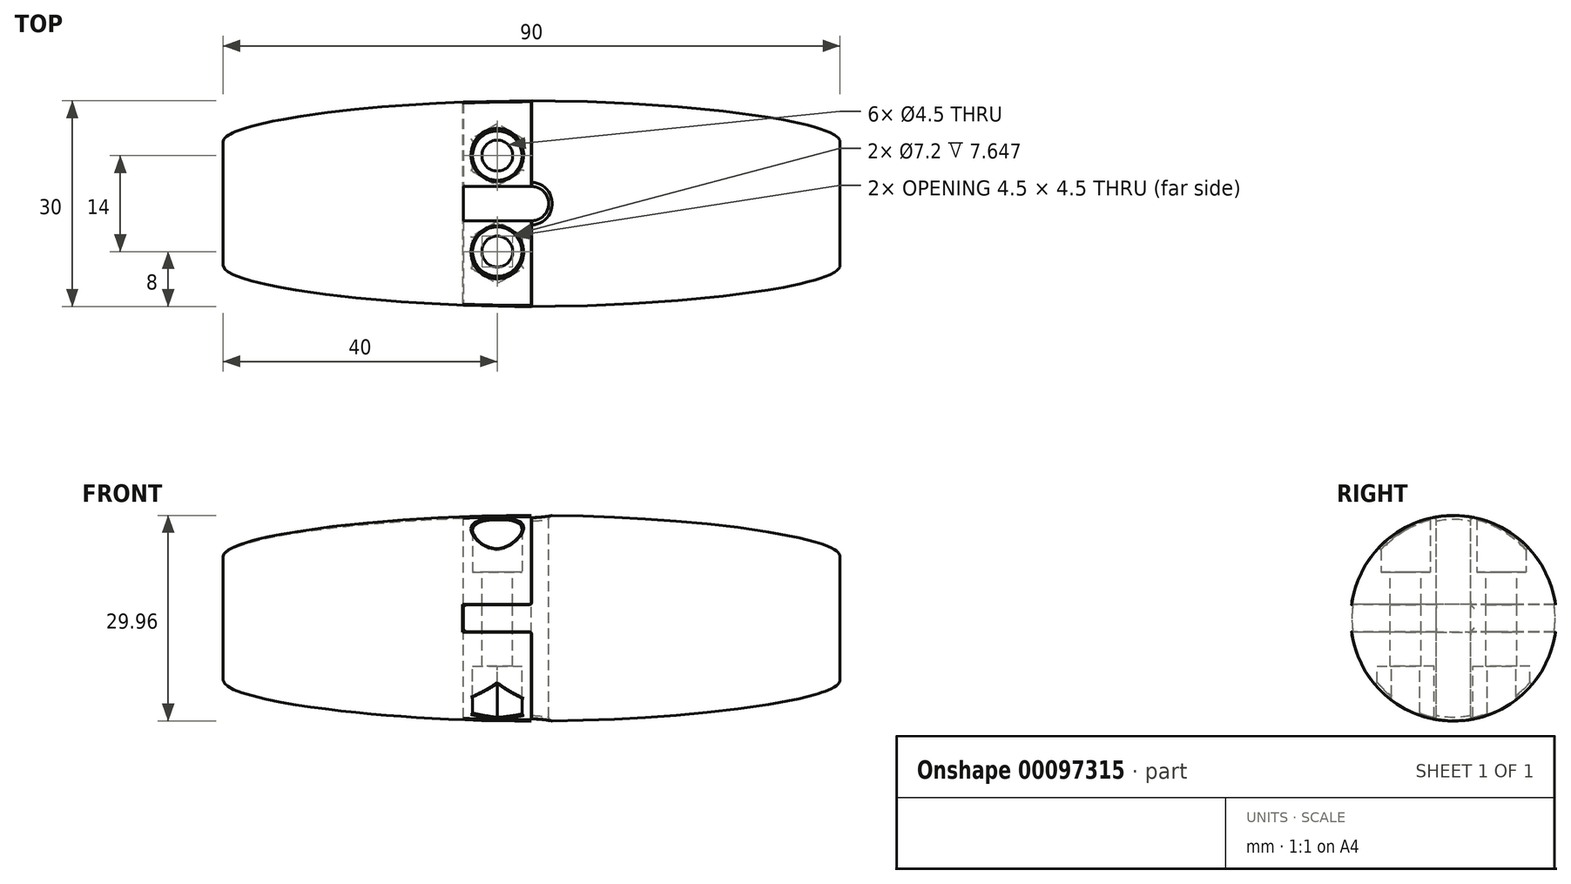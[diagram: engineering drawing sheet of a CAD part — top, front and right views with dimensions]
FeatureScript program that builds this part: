
annotation { "Feature Type Name" : "Feature", "Feature Type Description" : "" }
export const myFeature = defineFeature(function(context is Context, id is Id, definition is map)
    precondition{}
    {
        {
            assignVariable(context, id + "F0", {"name" : "rL", "anyValue" : 0.5});
        }
        {
            var Q0;
            Q0=qCreatedBy(makeId("Front.planeOp"),FACE);
            var sketch = newSketch(context, id + "F1", { "sketchPlane" : qUnion([Q0])});
            skLineSegment(sketch, "E0", {"start": v(0, 0) * mm, "end": v(45, 0) * mm});
            skLineSegment(sketch, "E1", {"start": v(45, 0) * mm, "end": v(45, 9) * mm});
            skLineSegment(sketch, "E2", {"start": v(0, 0) * mm, "end": v(0, 15) * mm, "construction": true});
            skLineSegment(sketch, "E3.MirrorCS", {"start": v(-45, 0) * mm, "end": v(-45, 9) * mm});
            skLineSegment(sketch, "E4.MirrorCS", {"start": v(0, 0) * mm, "end": v(-45, 0) * mm});
            skLineSegment(sketch, "E5", {"start": v(0, 15) * mm, "end": v(45, 15) * mm, "construction": true});
            skFitSpline(sketch, "E6", {"points": [v(-45, 9) * mm, v(0, 15) * mm, v(45, 9) * mm], "startDerivative": vector(0, 18) * mm, "endDerivative": vector(0, -18) * mm});
            skSolve(sketch);
        }
        {
            var Q0;
            Q0 = qSketchRegion(id + "F1", true);
            var Q1;
            Q1=sQuery(id+"F1.wireOp",EDGE,"E4.MirrorCS");
            revolve(context, id + "F2", {"entities" : qUnion([Q0]), "axis" : qUnion([Q1]), "revolveType" : RevolveType.FULL});
        }
        {
            var Q0;
            Q0=qCreatedBy(makeId("Top.planeOp"),FACE);
            var sketch = newSketch(context, id + "F3", { "sketchPlane" : qUnion([Q0])});
            skCircle(sketch, "E7", {"center": v(0, 0) * mm, "radius": 2.5 * mm});
            skSolve(sketch);
        }
        {
            var Q0;
            Q0 = qSketchRegion(id + "F3", true);
            extrude(context, id + "F4", {"entities" : qUnion([Q0]), "operationType" : NewBodyOperationType.REMOVE, "endBound" : BoundingType.THROUGH_ALL, "oppositeDirection" : true, "depth" : 25 * mm, "hasSecondDirection" : true, "secondDirectionBound" : SecondDirectionBoundingType.THROUGH_ALL, "secondDirectionOppositeDirection" : false, "secondDirectionDepth" : 25 * mm});
        }
        {
            var Q0;
            Q0=qCreatedBy(makeId("Front.planeOp"),FACE);
            var sketch = newSketch(context, id + "F5", { "sketchPlane" : qUnion([Q0])});
            skLineSegment(sketch, "E8", {"start": v(0, 14.99) * mm, "end": v(0, 2) * mm});
            skLineSegment(sketch, "E9", {"start": v(0, 2) * mm, "end": v(-10, 2) * mm});
            skLineSegment(sketch, "E10", {"start": v(-10, 2) * mm, "end": v(-10, -2) * mm});
            skLineSegment(sketch, "E11", {"start": v(-10, -2) * mm, "end": v(0, -2) * mm});
            skLineSegment(sketch, "E12", {"start": v(0, -2) * mm, "end": v(0, -14.99) * mm});
            skFitSpline(sketch, "E13", {"points": [v(45, -8) * mm, v(45, -11) * mm, v(0, -14) * mm, v(-45, -11) * mm, v(-45, -8) * mm], "construction": true});
            skFitSpline(sketch, "E14", {"points": [v(-45, 8) * mm, v(-45, 11) * mm, v(0, 14) * mm, v(45, 11) * mm, v(45, 8) * mm], "construction": true});
            skFitSpline(sketch, "E15", {"points": [v(-45, 8) * mm, v(-45, 11) * mm, v(0, 14) * mm, v(45, 11) * mm, v(45, 8) * mm], "construction": true});
            skFitSpline(sketch, "E16", {"points": [v(45, -8) * mm, v(45, -11) * mm, v(0, -14) * mm, v(-45, -11) * mm, v(-45, -8) * mm], "construction": true});
            skLineSegment(sketch, "E17.0", {"start": v(-0.05, -2.05) * mm, "end": v(-0.05, -14.99) * mm});
            skLineSegment(sketch, "E17.1", {"start": v(-0.05, 14.99) * mm, "end": v(-0.05, 2.05) * mm});
            skLineSegment(sketch, "E17.2", {"start": v(-0.05, 2.05) * mm, "end": v(-10.05, 2.05) * mm});
            skLineSegment(sketch, "E17.3", {"start": v(-10.05, 2.05) * mm, "end": v(-10.05, -2.05) * mm});
            skLineSegment(sketch, "E17.4", {"start": v(-10.05, -2.05) * mm, "end": v(-0.05, -2.05) * mm});
            skLineSegment(sketch, "E18.0", {"start": v(0.05, -1.95) * mm, "end": v(0.05, -14.99) * mm});
            skLineSegment(sketch, "E18.1", {"start": v(0.05, 14.99) * mm, "end": v(0.05, 1.95) * mm});
            skLineSegment(sketch, "E18.2", {"start": v(0.05, 1.95) * mm, "end": v(-9.95, 1.95) * mm});
            skLineSegment(sketch, "E18.3", {"start": v(-9.95, 1.95) * mm, "end": v(-9.95, -1.95) * mm});
            skLineSegment(sketch, "E18.4", {"start": v(-9.95, -1.95) * mm, "end": v(0.05, -1.95) * mm});
            skLineSegment(sketch, "E19", {"start": v(-0.05, -14.99) * mm, "end": v(0.05, -14.99) * mm});
            skLineSegment(sketch, "E20", {"start": v(-0.05, 14.99) * mm, "end": v(0.05, 14.99) * mm});
            skSolve(sketch);
        }
        {
            var Q0;
            Q0 = qSketchRegion(id + "F5", true);
            extrude(context, id + "F6", {"entities" : qUnion([Q0]), "operationType" : NewBodyOperationType.REMOVE, "endBound" : BoundingType.THROUGH_ALL, "oppositeDirection" : true, "depth" : 25 * mm, "hasSecondDirection" : true, "secondDirectionBound" : SecondDirectionBoundingType.THROUGH_ALL, "secondDirectionOppositeDirection" : false, "secondDirectionDepth" : 25 * mm});
        }
        {
            var Q0;
            Q0=qCreatedBy(makeId("Top.planeOp"),FACE);
            var sketch = newSketch(context, id + "F7", { "sketchPlane" : qUnion([Q0])});
            skArc(sketch, "E21.0", {"start": v(0, -2.5) * mm, "mid": v(2.5, -0.03) * mm, "end": v(0.05, 2.5) * mm});
            skLineSegment(sketch, "E22", {"start": v(0.05, 2.5) * mm, "end": v(-9.95, 2.5) * mm});
            skLineSegment(sketch, "E23", {"start": v(-9.95, 2.5) * mm, "end": v(-9.95, -2.5) * mm});
            skLineSegment(sketch, "E24", {"start": v(-9.95, -2.5) * mm, "end": v(0, -2.5) * mm});
            skSolve(sketch);
        }
        {
            var Q0;
            Q0 = qSketchRegion(id + "F7", true);
            extrude(context, id + "F8", {"entities" : qUnion([Q0]), "operationType" : NewBodyOperationType.REMOVE, "oppositeDirection" : true, "depth" : 25 * mm, "hasSecondDirection" : true, "secondDirectionOppositeDirection" : false, "secondDirectionDepth" : 25 * mm});
        }
        {
            var Q0;
            Q0=qCreatedBy(makeId("Top.planeOp"),FACE);
            var sketch = newSketch(context, id + "F9", { "sketchPlane" : qUnion([Q0])});
            skCircle(sketch, "E25", {"center": v(-5, -7) * mm, "radius": 2.25 * mm});
            skCircle(sketch, "E26", {"center": v(-5, 7) * mm, "radius": 2.25 * mm});
            skCircle(sketch, "E27", {"center": v(-5, -7) * mm, "radius": 3.5 * mm, "construction": true});
            skLineSegment(sketch, "E28", {"start": v(0, 0) * mm, "end": v(-30, 0) * mm, "construction": true});
            skSolve(sketch);
        }
        {
            var Q0;
            Q0 = qSketchRegion(id + "F9", true);
            extrude(context, id + "F10", {"entities" : qUnion([Q0]), "operationType" : NewBodyOperationType.REMOVE, "oppositeDirection" : true, "depth" : 25 * mm, "hasSecondDirection" : true, "secondDirectionOppositeDirection" : false, "secondDirectionDepth" : 25 * mm});
        }
        {
            var Q0;
            Q0=qCreatedBy(makeId("Top.planeOp"),FACE);
            cPlane(context, id + "F11", {"entities" : qUnion([Q0]), "cplaneType" : CPlaneType.OFFSET, "offset" : (5.2 + 1.78) * mm, "oppositeDirection" : true, "width" : 150 * mm, "height" : 150 * mm});
        }
        {
            var Q0;
            Q0=qCreatedBy(id+"F11.planeOp",FACE);
            var sketch = newSketch(context, id + "F12", { "sketchPlane" : qUnion([Q0])});
            skCircle(sketch, "E29.0", {"center": v(-5, -7) * mm, "radius": 2.25 * mm, "construction": true});
            skCircle(sketch, "E29.1", {"center": v(-5, 7) * mm, "radius": 2.25 * mm, "construction": true});
            skCircle(sketch, "E30.cCircle", {"center": v(-5, -7) * mm, "radius": 3.6 * mm, "construction": true});
            skLineSegment(sketch, "E30.0", {"start": v(-1.4, -4.92) * mm, "end": v(-1.4, -9.08) * mm});
            skLineSegment(sketch, "E30.1", {"start": v(-1.4, -9.08) * mm, "end": v(-5, -11.16) * mm});
            skLineSegment(sketch, "E30.2", {"start": v(-5, -11.16) * mm, "end": v(-8.6, -9.08) * mm});
            skLineSegment(sketch, "E30.3", {"start": v(-8.6, -9.08) * mm, "end": v(-8.6, -4.92) * mm});
            skLineSegment(sketch, "E30.4", {"start": v(-8.6, -4.92) * mm, "end": v(-5, -2.84) * mm});
            skLineSegment(sketch, "E30.5", {"start": v(-5, -2.84) * mm, "end": v(-1.4, -4.92) * mm});
            skPoint(sketch, "E30.0.midPoint", {"position": v(-1.4, -7) * mm});
            skCircle(sketch, "E31.cCircle", {"center": v(-5, 7) * mm, "radius": 3.6 * mm, "construction": true});
            skLineSegment(sketch, "E31.0", {"start": v(-1.4, 9.08) * mm, "end": v(-1.4, 4.92) * mm});
            skLineSegment(sketch, "E31.1", {"start": v(-1.4, 4.92) * mm, "end": v(-5, 2.84) * mm});
            skLineSegment(sketch, "E31.2", {"start": v(-5, 2.84) * mm, "end": v(-8.6, 4.92) * mm});
            skLineSegment(sketch, "E31.3", {"start": v(-8.6, 4.92) * mm, "end": v(-8.6, 9.08) * mm});
            skLineSegment(sketch, "E31.4", {"start": v(-8.6, 9.08) * mm, "end": v(-5, 11.16) * mm});
            skLineSegment(sketch, "E31.5", {"start": v(-5, 11.16) * mm, "end": v(-1.4, 9.08) * mm});
            skPoint(sketch, "E31.0.midPoint", {"position": v(-1.4, 7) * mm});
            skSolve(sketch);
        }
        {
            var Q0;
            Q0 = qSketchRegion(id + "F12", true);
            extrude(context, id + "F13", {"entities" : qUnion([Q0]), "operationType" : NewBodyOperationType.REMOVE, "oppositeDirection" : true, "depth" : 25 * mm});
        }
        {
            var Q0;
            Q0=qCreatedBy(makeId("Top.planeOp"),FACE);
            cPlane(context, id + "F14", {"entities" : qUnion([Q0]), "cplaneType" : CPlaneType.OFFSET, "offset" : (6.05 + 0.67) * mm, "width" : 150 * mm, "height" : 150 * mm});
        }
        {
            var Q0;
            Q0=qCreatedBy(id+"F14.planeOp",FACE);
            var sketch = newSketch(context, id + "F15", { "sketchPlane" : qUnion([Q0])});
            skCircle(sketch, "E32.0", {"center": v(-5, -7) * mm, "radius": 2.25 * mm, "construction": true});
            skCircle(sketch, "E32.1", {"center": v(-5, 7) * mm, "radius": 2.25 * mm, "construction": true});
            skCircle(sketch, "E33", {"center": v(-5, -7) * mm, "radius": 3.6 * mm});
            skCircle(sketch, "E34", {"center": v(-5, 7) * mm, "radius": 3.6 * mm});
            skSolve(sketch);
        }
        {
            var Q0;
            Q0 = qSketchRegion(id + "F15", true);
            extrude(context, id + "F16", {"entities" : qUnion([Q0]), "operationType" : NewBodyOperationType.REMOVE, "depth" : 25 * mm});
        }
        {
            var Q0;
            Q0=makeQuery(id+"F6.boolean.opBoolean","COPY",EDGE,{"disambiguationData":[OD(0.0)],"derivedFrom":makeQuery(id+"F6.opExtrude","SWEPT_EDGE",EDGE,{"disambiguationData":[OSD([sQuery(id+"F5.wireOp",EDGE,"E17.0"),sQuery(id+"F5.wireOp",EDGE,"E17.4")])]})});
            var Q1;
            Q1=makeQuery(id+"F6.boolean.opBoolean","COPY",EDGE,{"disambiguationData":[OD(1.0)],"derivedFrom":makeQuery(id+"F6.opExtrude","SWEPT_EDGE",EDGE,{"disambiguationData":[OSD([sQuery(id+"F5.wireOp",EDGE,"E17.0"),sQuery(id+"F5.wireOp",EDGE,"E17.4")])]})});
            var Q2;
            Q2=makeQuery(id+"F6.boolean.opBoolean","COPY",EDGE,{"derivedFrom":makeQuery(id+"F6.opExtrude","SWEPT_EDGE",EDGE,{"disambiguationData":[OSD([sQuery(id+"F5.wireOp",EDGE,"E17.3"),sQuery(id+"F5.wireOp",EDGE,"E17.4")])]})});
            var Q3;
            Q3=makeQuery(id+"F6.boolean.opBoolean","COPY",EDGE,{"derivedFrom":makeQuery(id+"F6.opExtrude","SWEPT_EDGE",EDGE,{"disambiguationData":[OSD([sQuery(id+"F5.wireOp",EDGE,"E17.2"),sQuery(id+"F5.wireOp",EDGE,"E17.3")])]})});
            var Q4;
            Q4=makeQuery(id+"F6.boolean.opBoolean","COPY",EDGE,{"disambiguationData":[OD(0.0)],"derivedFrom":makeQuery(id+"F6.opExtrude","SWEPT_EDGE",EDGE,{"disambiguationData":[OSD([sQuery(id+"F5.wireOp",EDGE,"E17.1"),sQuery(id+"F5.wireOp",EDGE,"E17.2")])]})});
            var Q5;
            Q5=makeQuery(id+"F6.boolean.opBoolean","COPY",EDGE,{"disambiguationData":[OD(1.0)],"derivedFrom":makeQuery(id+"F6.opExtrude","SWEPT_EDGE",EDGE,{"disambiguationData":[OSD([sQuery(id+"F5.wireOp",EDGE,"E17.1"),sQuery(id+"F5.wireOp",EDGE,"E17.2")])]})});
            var Q6;
            {var subQ0=makeQuery(id+"F2.opRevolve","SWEPT_FACE",FACE,{"disambiguationData":[OSD([sQuery(id+"F1.wireOp",EDGE,"E6")])]});var subQ1=makeQuery(id+"F4.opExtrude","SWEPT_FACE",FACE,{"disambiguationData":[OSD([sQuery(id+"F3.wireOp",EDGE,"E7")])]});Q6=makeQuery(id+"F6.boolean.opBoolean","SPLIT",EDGE,{"disambiguationData":[TD([makeQuery(id+"F6.opExtrude","SWEPT_FACE",FACE,{"disambiguationData":[OSD([sQuery(id+"F5.wireOp",EDGE,"E17.1")])]})])],"derivedFrom":makeQuery(id+"F4.boolean.opBoolean","INTERSECT",EDGE,{"disambiguationData":[OD(1.0)],"derivedFrom":[subQ0,subQ1]})});}
            var Q7;
            {var subQ0=makeQuery(id+"F2.opRevolve","SWEPT_FACE",FACE,{"disambiguationData":[OSD([sQuery(id+"F1.wireOp",EDGE,"E6")])]});var subQ1=makeQuery(id+"F4.opExtrude","SWEPT_FACE",FACE,{"disambiguationData":[OSD([sQuery(id+"F3.wireOp",EDGE,"E7")])]});Q7=makeQuery(id+"F6.boolean.opBoolean","SPLIT",EDGE,{"disambiguationData":[TD([makeQuery(id+"F6.opExtrude","SWEPT_FACE",FACE,{"disambiguationData":[OSD([sQuery(id+"F5.wireOp",EDGE,"E17.0")])]})])],"derivedFrom":makeQuery(id+"F4.boolean.opBoolean","INTERSECT",EDGE,{"disambiguationData":[OD(0.0)],"derivedFrom":[subQ0,subQ1]})});}
            var Q8;
            {var subQ0=makeQuery(id+"F2.opRevolve","SWEPT_FACE",FACE,{"disambiguationData":[OSD([sQuery(id+"F1.wireOp",EDGE,"E6")])]});var subQ1=makeQuery(id+"F4.opExtrude","SWEPT_FACE",FACE,{"disambiguationData":[OSD([sQuery(id+"F3.wireOp",EDGE,"E7")])]});Q8=makeQuery(id+"F6.boolean.opBoolean","SPLIT",EDGE,{"disambiguationData":[TD([makeQuery(id+"F6.opExtrude","SWEPT_FACE",FACE,{"disambiguationData":[OSD([sQuery(id+"F5.wireOp",EDGE,"E18.0")])]})])],"derivedFrom":makeQuery(id+"F4.boolean.opBoolean","INTERSECT",EDGE,{"disambiguationData":[OD(0.0)],"derivedFrom":[subQ0,subQ1]})});}
            var Q9;
            {var subQ0=makeQuery(id+"F2.opRevolve","SWEPT_FACE",FACE,{"disambiguationData":[OSD([sQuery(id+"F1.wireOp",EDGE,"E6")])]});var subQ1=makeQuery(id+"F4.opExtrude","SWEPT_FACE",FACE,{"disambiguationData":[OSD([sQuery(id+"F3.wireOp",EDGE,"E7")])]});Q9=makeQuery(id+"F6.boolean.opBoolean","SPLIT",EDGE,{"disambiguationData":[TD([makeQuery(id+"F6.opExtrude","SWEPT_FACE",FACE,{"disambiguationData":[OSD([sQuery(id+"F5.wireOp",EDGE,"E18.1")])]})])],"derivedFrom":makeQuery(id+"F4.boolean.opBoolean","INTERSECT",EDGE,{"disambiguationData":[OD(1.0)],"derivedFrom":[subQ0,subQ1]})});}
            var Q10;
            Q10=makeQuery(id+"F6.boolean.opBoolean","COPY",EDGE,{"disambiguationData":[OD(0.0)],"derivedFrom":makeQuery(id+"F6.opExtrude","SWEPT_EDGE",EDGE,{"disambiguationData":[OSD([sQuery(id+"F5.wireOp",EDGE,"E18.1"),sQuery(id+"F5.wireOp",EDGE,"E18.2")])]})});
            var Q11;
            {var subQ0=sQuery(id+"F5.wireOp",EDGE,"E18.2");var subQ1=sQuery(id+"F5.wireOp",EDGE,"E18.3");Q11=makeQuery(id+"F8.boolean.opBoolean","SPLIT",EDGE,{"disambiguationData":[TD([makeQuery(id+"F8.opExtrude","SWEPT_FACE",FACE,{"disambiguationData":[OSD([sQuery(id+"F7.wireOp",EDGE,"E24")])]})])],"derivedFrom":makeQuery(id+"F6.boolean.opBoolean","COPY",EDGE,{"derivedFrom":makeQuery(id+"F6.opExtrude","SWEPT_EDGE",EDGE,{"disambiguationData":[OSD([subQ0,subQ1])]})})});}
            var Q12;
            {var subQ0=sQuery(id+"F5.wireOp",EDGE,"E18.3");var subQ1=sQuery(id+"F5.wireOp",EDGE,"E18.4");Q12=makeQuery(id+"F8.boolean.opBoolean","SPLIT",EDGE,{"disambiguationData":[TD([makeQuery(id+"F8.opExtrude","SWEPT_FACE",FACE,{"disambiguationData":[OSD([sQuery(id+"F7.wireOp",EDGE,"E24")])]})])],"derivedFrom":makeQuery(id+"F6.boolean.opBoolean","COPY",EDGE,{"derivedFrom":makeQuery(id+"F6.opExtrude","SWEPT_EDGE",EDGE,{"disambiguationData":[OSD([subQ0,subQ1])]})})});}
            var Q13;
            Q13=makeQuery(id+"F6.boolean.opBoolean","COPY",EDGE,{"disambiguationData":[OD(1.0)],"derivedFrom":makeQuery(id+"F6.opExtrude","SWEPT_EDGE",EDGE,{"disambiguationData":[OSD([sQuery(id+"F5.wireOp",EDGE,"E18.1"),sQuery(id+"F5.wireOp",EDGE,"E18.2")])]})});
            var Q14;
            {var subQ0=sQuery(id+"F5.wireOp",EDGE,"E18.2");var subQ1=sQuery(id+"F5.wireOp",EDGE,"E18.3");Q14=makeQuery(id+"F8.boolean.opBoolean","SPLIT",EDGE,{"disambiguationData":[TD([makeQuery(id+"F8.opExtrude","SWEPT_FACE",FACE,{"disambiguationData":[OSD([sQuery(id+"F7.wireOp",EDGE,"E22")])]})])],"derivedFrom":makeQuery(id+"F6.boolean.opBoolean","COPY",EDGE,{"derivedFrom":makeQuery(id+"F6.opExtrude","SWEPT_EDGE",EDGE,{"disambiguationData":[OSD([subQ0,subQ1])]})})});}
            var Q15;
            {var subQ0=sQuery(id+"F5.wireOp",EDGE,"E18.3");var subQ1=sQuery(id+"F5.wireOp",EDGE,"E18.4");Q15=makeQuery(id+"F8.boolean.opBoolean","SPLIT",EDGE,{"disambiguationData":[TD([makeQuery(id+"F8.opExtrude","SWEPT_FACE",FACE,{"disambiguationData":[OSD([sQuery(id+"F7.wireOp",EDGE,"E22")])]})])],"derivedFrom":makeQuery(id+"F6.boolean.opBoolean","COPY",EDGE,{"derivedFrom":makeQuery(id+"F6.opExtrude","SWEPT_EDGE",EDGE,{"disambiguationData":[OSD([subQ0,subQ1])]})})});}
            var Q16;
            Q16=makeQuery(id+"F6.boolean.opBoolean","COPY",EDGE,{"disambiguationData":[OD(1.0)],"derivedFrom":makeQuery(id+"F6.opExtrude","SWEPT_EDGE",EDGE,{"disambiguationData":[OSD([sQuery(id+"F5.wireOp",EDGE,"E18.0"),sQuery(id+"F5.wireOp",EDGE,"E18.4")])]})});
            var Q17;
            Q17=makeQuery(id+"F6.boolean.opBoolean","COPY",EDGE,{"disambiguationData":[OD(0.0)],"derivedFrom":makeQuery(id+"F6.opExtrude","SWEPT_EDGE",EDGE,{"disambiguationData":[OSD([sQuery(id+"F5.wireOp",EDGE,"E18.0"),sQuery(id+"F5.wireOp",EDGE,"E18.4")])]})});
            var Q18;
            Q18=makeQuery(id+"F8.boolean.opBoolean","COPY",EDGE,{"derivedFrom":makeQuery(id+"F8.opExtrude","SWEPT_EDGE",EDGE,{"disambiguationData":[OSD([sQuery(id+"F7.wireOp",EDGE,"E23"),sQuery(id+"F7.wireOp",EDGE,"E24")])]})});
            var Q19;
            Q19=makeQuery(id+"F8.boolean.opBoolean","COPY",EDGE,{"derivedFrom":makeQuery(id+"F8.opExtrude","SWEPT_EDGE",EDGE,{"disambiguationData":[OSD([sQuery(id+"F7.wireOp",EDGE,"E22"),sQuery(id+"F7.wireOp",EDGE,"E23")])]})});
            fillet(context, id + "F17", {"entities" : qUnion([Q0, Q1, Q2, Q3, Q4, Q5, Q6, Q7, Q8, Q9, Q10, Q11, Q12, Q13, Q14, Q15, Q16, Q17, Q18, Q19]), "radius" : (getVariable(context, 'rL')) * mm, "tangentPropagation" : true, "allowEdgeOverflow" : false});
        }
        {
            var Q0;
            Q0=makeQuery(id+"F13.boolean.opBoolean","INTERSECT",EDGE,{"derivedFrom":[makeQuery(id+"F6.boolean.opBoolean","SPLIT",FACE,{"disambiguationData":[TD([makeQuery(id+"F2.opRevolve","SWEPT_FACE",FACE,{"disambiguationData":[OSD([sQuery(id+"F1.wireOp",EDGE,"E3.MirrorCS")])]})])],"derivedFrom":makeQuery(id+"F2.opRevolve","SWEPT_FACE",FACE,{"disambiguationData":[OSD([sQuery(id+"F1.wireOp",EDGE,"E6")])]})}),makeQuery(id+"F13.opExtrude","SWEPT_FACE",FACE,{"disambiguationData":[OSD([sQuery(id+"F12.wireOp",EDGE,"E31.1")])]})]});
            var Q1;
            Q1=makeQuery(id+"F13.boolean.opBoolean","INTERSECT",EDGE,{"derivedFrom":[makeQuery(id+"F6.boolean.opBoolean","SPLIT",FACE,{"disambiguationData":[TD([makeQuery(id+"F2.opRevolve","SWEPT_FACE",FACE,{"disambiguationData":[OSD([sQuery(id+"F1.wireOp",EDGE,"E3.MirrorCS")])]})])],"derivedFrom":makeQuery(id+"F2.opRevolve","SWEPT_FACE",FACE,{"disambiguationData":[OSD([sQuery(id+"F1.wireOp",EDGE,"E6")])]})}),makeQuery(id+"F13.opExtrude","SWEPT_FACE",FACE,{"disambiguationData":[OSD([sQuery(id+"F12.wireOp",EDGE,"E31.0")])]})]});
            var Q2;
            Q2=makeQuery(id+"F13.boolean.opBoolean","INTERSECT",EDGE,{"derivedFrom":[makeQuery(id+"F6.boolean.opBoolean","SPLIT",FACE,{"disambiguationData":[TD([makeQuery(id+"F2.opRevolve","SWEPT_FACE",FACE,{"disambiguationData":[OSD([sQuery(id+"F1.wireOp",EDGE,"E3.MirrorCS")])]})])],"derivedFrom":makeQuery(id+"F2.opRevolve","SWEPT_FACE",FACE,{"disambiguationData":[OSD([sQuery(id+"F1.wireOp",EDGE,"E6")])]})}),makeQuery(id+"F13.opExtrude","SWEPT_FACE",FACE,{"disambiguationData":[OSD([sQuery(id+"F12.wireOp",EDGE,"E31.5")])]})]});
            var Q3;
            Q3=makeQuery(id+"F13.boolean.opBoolean","INTERSECT",EDGE,{"derivedFrom":[makeQuery(id+"F6.boolean.opBoolean","SPLIT",FACE,{"disambiguationData":[TD([makeQuery(id+"F2.opRevolve","SWEPT_FACE",FACE,{"disambiguationData":[OSD([sQuery(id+"F1.wireOp",EDGE,"E3.MirrorCS")])]})])],"derivedFrom":makeQuery(id+"F2.opRevolve","SWEPT_FACE",FACE,{"disambiguationData":[OSD([sQuery(id+"F1.wireOp",EDGE,"E6")])]})}),makeQuery(id+"F13.opExtrude","SWEPT_FACE",FACE,{"disambiguationData":[OSD([sQuery(id+"F12.wireOp",EDGE,"E31.4")])]})]});
            var Q4;
            Q4=makeQuery(id+"F13.boolean.opBoolean","INTERSECT",EDGE,{"derivedFrom":[makeQuery(id+"F6.boolean.opBoolean","SPLIT",FACE,{"disambiguationData":[TD([makeQuery(id+"F2.opRevolve","SWEPT_FACE",FACE,{"disambiguationData":[OSD([sQuery(id+"F1.wireOp",EDGE,"E3.MirrorCS")])]})])],"derivedFrom":makeQuery(id+"F2.opRevolve","SWEPT_FACE",FACE,{"disambiguationData":[OSD([sQuery(id+"F1.wireOp",EDGE,"E6")])]})}),makeQuery(id+"F13.opExtrude","SWEPT_FACE",FACE,{"disambiguationData":[OSD([sQuery(id+"F12.wireOp",EDGE,"E31.3")])]})]});
            var Q5;
            Q5=makeQuery(id+"F13.boolean.opBoolean","INTERSECT",EDGE,{"derivedFrom":[makeQuery(id+"F6.boolean.opBoolean","SPLIT",FACE,{"disambiguationData":[TD([makeQuery(id+"F2.opRevolve","SWEPT_FACE",FACE,{"disambiguationData":[OSD([sQuery(id+"F1.wireOp",EDGE,"E3.MirrorCS")])]})])],"derivedFrom":makeQuery(id+"F2.opRevolve","SWEPT_FACE",FACE,{"disambiguationData":[OSD([sQuery(id+"F1.wireOp",EDGE,"E6")])]})}),makeQuery(id+"F13.opExtrude","SWEPT_FACE",FACE,{"disambiguationData":[OSD([sQuery(id+"F12.wireOp",EDGE,"E31.2")])]})]});
            var Q6;
            Q6=makeQuery(id+"F13.boolean.opBoolean","INTERSECT",EDGE,{"derivedFrom":[makeQuery(id+"F6.boolean.opBoolean","SPLIT",FACE,{"disambiguationData":[TD([makeQuery(id+"F2.opRevolve","SWEPT_FACE",FACE,{"disambiguationData":[OSD([sQuery(id+"F1.wireOp",EDGE,"E3.MirrorCS")])]})])],"derivedFrom":makeQuery(id+"F2.opRevolve","SWEPT_FACE",FACE,{"disambiguationData":[OSD([sQuery(id+"F1.wireOp",EDGE,"E6")])]})}),makeQuery(id+"F13.opExtrude","SWEPT_FACE",FACE,{"disambiguationData":[OSD([sQuery(id+"F12.wireOp",EDGE,"E30.4")])]})]});
            var Q7;
            Q7=makeQuery(id+"F13.boolean.opBoolean","INTERSECT",EDGE,{"derivedFrom":[makeQuery(id+"F6.boolean.opBoolean","SPLIT",FACE,{"disambiguationData":[TD([makeQuery(id+"F2.opRevolve","SWEPT_FACE",FACE,{"disambiguationData":[OSD([sQuery(id+"F1.wireOp",EDGE,"E3.MirrorCS")])]})])],"derivedFrom":makeQuery(id+"F2.opRevolve","SWEPT_FACE",FACE,{"disambiguationData":[OSD([sQuery(id+"F1.wireOp",EDGE,"E6")])]})}),makeQuery(id+"F13.opExtrude","SWEPT_FACE",FACE,{"disambiguationData":[OSD([sQuery(id+"F12.wireOp",EDGE,"E30.3")])]})]});
            var Q8;
            Q8=makeQuery(id+"F13.boolean.opBoolean","INTERSECT",EDGE,{"derivedFrom":[makeQuery(id+"F6.boolean.opBoolean","SPLIT",FACE,{"disambiguationData":[TD([makeQuery(id+"F2.opRevolve","SWEPT_FACE",FACE,{"disambiguationData":[OSD([sQuery(id+"F1.wireOp",EDGE,"E3.MirrorCS")])]})])],"derivedFrom":makeQuery(id+"F2.opRevolve","SWEPT_FACE",FACE,{"disambiguationData":[OSD([sQuery(id+"F1.wireOp",EDGE,"E6")])]})}),makeQuery(id+"F13.opExtrude","SWEPT_FACE",FACE,{"disambiguationData":[OSD([sQuery(id+"F12.wireOp",EDGE,"E30.2")])]})]});
            var Q9;
            Q9=makeQuery(id+"F13.boolean.opBoolean","INTERSECT",EDGE,{"derivedFrom":[makeQuery(id+"F6.boolean.opBoolean","SPLIT",FACE,{"disambiguationData":[TD([makeQuery(id+"F2.opRevolve","SWEPT_FACE",FACE,{"disambiguationData":[OSD([sQuery(id+"F1.wireOp",EDGE,"E3.MirrorCS")])]})])],"derivedFrom":makeQuery(id+"F2.opRevolve","SWEPT_FACE",FACE,{"disambiguationData":[OSD([sQuery(id+"F1.wireOp",EDGE,"E6")])]})}),makeQuery(id+"F13.opExtrude","SWEPT_FACE",FACE,{"disambiguationData":[OSD([sQuery(id+"F12.wireOp",EDGE,"E30.1")])]})]});
            var Q10;
            Q10=makeQuery(id+"F13.boolean.opBoolean","INTERSECT",EDGE,{"derivedFrom":[makeQuery(id+"F6.boolean.opBoolean","SPLIT",FACE,{"disambiguationData":[TD([makeQuery(id+"F2.opRevolve","SWEPT_FACE",FACE,{"disambiguationData":[OSD([sQuery(id+"F1.wireOp",EDGE,"E3.MirrorCS")])]})])],"derivedFrom":makeQuery(id+"F2.opRevolve","SWEPT_FACE",FACE,{"disambiguationData":[OSD([sQuery(id+"F1.wireOp",EDGE,"E6")])]})}),makeQuery(id+"F13.opExtrude","SWEPT_FACE",FACE,{"disambiguationData":[OSD([sQuery(id+"F12.wireOp",EDGE,"E30.0")])]})]});
            var Q11;
            Q11=makeQuery(id+"F13.boolean.opBoolean","INTERSECT",EDGE,{"derivedFrom":[makeQuery(id+"F6.boolean.opBoolean","SPLIT",FACE,{"disambiguationData":[TD([makeQuery(id+"F2.opRevolve","SWEPT_FACE",FACE,{"disambiguationData":[OSD([sQuery(id+"F1.wireOp",EDGE,"E3.MirrorCS")])]})])],"derivedFrom":makeQuery(id+"F2.opRevolve","SWEPT_FACE",FACE,{"disambiguationData":[OSD([sQuery(id+"F1.wireOp",EDGE,"E6")])]})}),makeQuery(id+"F13.opExtrude","SWEPT_FACE",FACE,{"disambiguationData":[OSD([sQuery(id+"F12.wireOp",EDGE,"E30.5")])]})]});
            var Q12;
            Q12=makeQuery(id+"F16.boolean.opBoolean","INTERSECT",EDGE,{"derivedFrom":[makeQuery(id+"F6.boolean.opBoolean","SPLIT",FACE,{"disambiguationData":[TD([makeQuery(id+"F2.opRevolve","SWEPT_FACE",FACE,{"disambiguationData":[OSD([sQuery(id+"F1.wireOp",EDGE,"E3.MirrorCS")])]})])],"derivedFrom":makeQuery(id+"F2.opRevolve","SWEPT_FACE",FACE,{"disambiguationData":[OSD([sQuery(id+"F1.wireOp",EDGE,"E6")])]})}),makeQuery(id+"F16.opExtrude","SWEPT_FACE",FACE,{"disambiguationData":[OSD([sQuery(id+"F15.wireOp",EDGE,"E33")])]})]});
            var Q13;
            Q13=makeQuery(id+"F16.boolean.opBoolean","INTERSECT",EDGE,{"derivedFrom":[makeQuery(id+"F6.boolean.opBoolean","SPLIT",FACE,{"disambiguationData":[TD([makeQuery(id+"F2.opRevolve","SWEPT_FACE",FACE,{"disambiguationData":[OSD([sQuery(id+"F1.wireOp",EDGE,"E3.MirrorCS")])]})])],"derivedFrom":makeQuery(id+"F2.opRevolve","SWEPT_FACE",FACE,{"disambiguationData":[OSD([sQuery(id+"F1.wireOp",EDGE,"E6")])]})}),makeQuery(id+"F16.opExtrude","SWEPT_FACE",FACE,{"disambiguationData":[OSD([sQuery(id+"F15.wireOp",EDGE,"E34")])]})]});
            fillet(context, id + "F18", {"entities" : qUnion([Q0, Q1, Q2, Q3, Q4, Q5, Q6, Q7, Q8, Q9, Q10, Q11, Q12, Q13]), "radius" : (getVariable(context, 'rL') / 2) * mm, "tangentPropagation" : true, "allowEdgeOverflow" : false});
        }
    });
